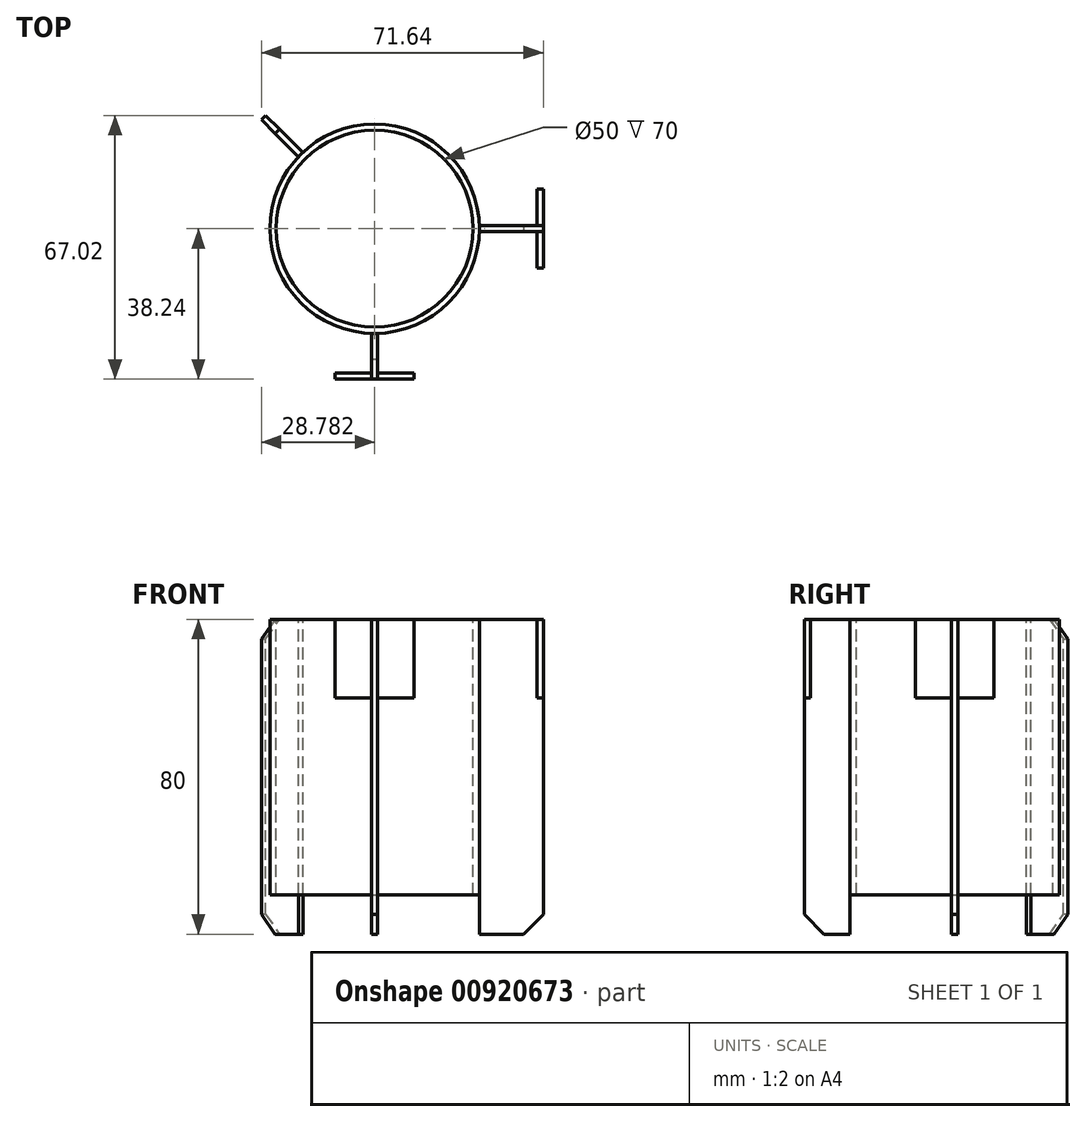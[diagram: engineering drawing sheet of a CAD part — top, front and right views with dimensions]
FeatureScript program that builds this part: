
annotation { "Feature Type Name" : "Feature", "Feature Type Description" : "" }
export const myFeature = defineFeature(function(context is Context, id is Id, definition is map)
    precondition{}
    {
        {
            var Q0;
            Q0=qCreatedBy(makeId("Top.planeOp"),FACE);
            var sketch = newSketch(context, id + "F0", { "sketchPlane" : qUnion([Q0])});
            skCircle(sketch, "E0", {"center": v(31.14, -33.92) * mm, "radius": 8 * mm});
            skLineSegment(sketch, "E1", {"start": v(31.14, -33.92) * mm, "end": v(-100.33, -33.92) * mm, "construction": true});
            skLineSegment(sketch, "E2", {"start": v(31.14, -33.92) * mm, "end": v(31.14, 79.64) * mm, "construction": true});
            skArc(sketch, "E3", {"start": v(30.64, 73.58) * mm, "mid": v(-43.22, 43.7) * mm, "end": v(-76.23, -28.8) * mm});
            skLineSegment(sketch, "E4", {"start": v(30.64, -25.94) * mm, "end": v(30.64, 73.58) * mm});
            skLineSegment(sketch, "E5", {"start": v(25, -28.8) * mm, "end": v(-76.23, -28.8) * mm});
            skArc(sketch, "E6", {"start": v(-76.23, -28.8) * mm, "mid": v(-76.32, -31.11) * mm, "end": v(-76.36, -33.42) * mm});
            skLineSegment(sketch, "E7", {"start": v(25, -28.8) * mm, "end": v(25, -28.8) * mm});
            skLineSegment(sketch, "E8.0", {"start": v(23.16, -27.2) * mm, "end": v(-74.54, -27.2) * mm});
            skArc(sketch, "E8.1", {"start": v(29.04, 71.96) * mm, "mid": v(-42.09, 42.58) * mm, "end": v(-74.54, -27.2) * mm});
            skLineSegment(sketch, "E8.2", {"start": v(29.04, -21.32) * mm, "end": v(29.04, 71.96) * mm});
            skCircle(sketch, "E9.0", {"center": v(31.14, -33.92) * mm, "radius": 9.6 * mm});
            skLineSegment(sketch, "E10", {"start": v(-69.87, 2.84) * mm, "end": v(-68.37, 2.3) * mm});
            skLineSegment(sketch, "E11", {"start": v(-58.85, -28.8) * mm, "end": v(-58.83, -27.19) * mm});
            skLineSegment(sketch, "E12", {"start": v(1.15, -28.8) * mm, "end": v(1.22, -27.2) * mm});
            skLineSegment(sketch, "E13", {"start": v(29.04, 0.62) * mm, "end": v(30.64, 0.73) * mm});
            skLineSegment(sketch, "E14", {"start": v(29.04, 60.67) * mm, "end": v(30.64, 60.7) * mm});
            skLineSegment(sketch, "E15", {"start": v(-5.62, 67.1) * mm, "end": v(-5.07, 65.6) * mm});
            skCircle(sketch, "E16", {"center": v(31.14, -33.92) * mm, "radius": 65 * mm, "construction": true});
            skLineSegment(sketch, "E17", {"start": v(31.14, -33.92) * mm, "end": v(-78.94, 76.16) * mm, "construction": true});
            skPoint(sketch, "E18", {"position": v(-14.82, 12.04) * mm});
            skCircle(sketch, "E19", {"center": v(-14.82, 12.04) * mm, "radius": 25 * mm});
            skCircle(sketch, "E20.0", {"center": v(-14.82, 12.04) * mm, "radius": 26.6 * mm});
            skLineSegment(sketch, "E21", {"start": v(-14.82, 12.04) * mm, "end": v(41.83, 12.04) * mm, "construction": true});
            skLineSegment(sketch, "E22", {"start": v(-14.82, 12.04) * mm, "end": v(-14.82, -37.35) * mm, "construction": true});
            skLineSegment(sketch, "E23", {"start": v(11.77, 12.84) * mm, "end": v(28.04, 12.84) * mm});
            skLineSegment(sketch, "E24", {"start": v(28.04, 12.84) * mm, "end": v(28.04, 11.24) * mm});
            skLineSegment(sketch, "E25", {"start": v(28.04, 11.24) * mm, "end": v(11.77, 11.24) * mm});
            skLineSegment(sketch, "E26", {"start": v(-14.02, -14.55) * mm, "end": v(-14.02, -26.2) * mm});
            skLineSegment(sketch, "E27", {"start": v(-14.02, -26.2) * mm, "end": v(-15.62, -26.2) * mm});
            skLineSegment(sketch, "E28", {"start": v(-15.62, -26.2) * mm, "end": v(-15.62, -14.55) * mm});
            skLineSegment(sketch, "E29", {"start": v(-34.18, 30.27) * mm, "end": v(-43.6, 39.69) * mm});
            skLineSegment(sketch, "E30", {"start": v(-43.6, 39.69) * mm, "end": v(-42.47, 40.82) * mm});
            skLineSegment(sketch, "E31", {"start": v(-42.47, 40.82) * mm, "end": v(-33.05, 31.4) * mm});
            skLineSegment(sketch, "E32", {"start": v(-46.34, 35.36) * mm, "end": v(-46.34, 35.36) * mm});
            skPoint(sketch, "E33", {"position": v(-14.82, -25.4) * mm});
            skLineSegment(sketch, "E34.bottom", {"start": v(-4.82, -26.2) * mm, "end": v(-24.82, -26.2) * mm});
            skLineSegment(sketch, "E34.top", {"start": v(-4.82, -24.6) * mm, "end": v(-24.82, -24.6) * mm});
            skLineSegment(sketch, "E34.left", {"start": v(-4.82, -26.2) * mm, "end": v(-4.82, -24.6) * mm});
            skLineSegment(sketch, "E34.right", {"start": v(-24.82, -26.2) * mm, "end": v(-24.82, -24.6) * mm});
            skPoint(sketch, "E35", {"position": v(27.24, 12.04) * mm});
            skLineSegment(sketch, "E36.bottom", {"start": v(28.04, 2.04) * mm, "end": v(26.44, 2.04) * mm});
            skLineSegment(sketch, "E36.top", {"start": v(28.04, 22.04) * mm, "end": v(26.44, 22.04) * mm});
            skLineSegment(sketch, "E36.left", {"start": v(28.04, 2.04) * mm, "end": v(28.04, 22.04) * mm});
            skLineSegment(sketch, "E36.right", {"start": v(26.44, 2.04) * mm, "end": v(26.44, 22.04) * mm});
            skSolve(sketch);
        }
        {
            var Q0;
            {var subQ0=sQuery(id+"F0.wireOp",EDGE,"E29");Q0=makeQuery(id+"F0.imprint","IMPRINT",FACE,{"disambiguationData":[TD([[makeQuery(id+"F0.imprint","IMPRINT",EDGE,{"derivedFrom":subQ0}),-1.0]])]});}
            var Q1;
            {var subQ0=sQuery(id+"F0.wireOp",EDGE,"E26");Q1=makeQuery(id+"F0.imprint","IMPRINT",FACE,{"disambiguationData":[TD([[makeQuery(id+"F0.imprint","IMPRINT",EDGE,{"derivedFrom":subQ0}),-1.0]])]});}
            var Q2;
            {var subQ0=sQuery(id+"F0.wireOp",EDGE,"E23");Q2=makeQuery(id+"F0.imprint","IMPRINT",FACE,{"disambiguationData":[TD([[makeQuery(id+"F0.imprint","IMPRINT",EDGE,{"derivedFrom":subQ0}),-1.0]])]});}
            extrude(context, id + "F1", {"entities" : qUnion([Q0, Q1, Q2]), "oppositeDirection" : true, "depth" : 80 * mm, "offsetDistance" : 25 * mm});
        }
        {
            var Q0;
            Q0=makeQuery(id+"F0.imprint","IMPRINT",FACE,{"disambiguationData":[TD([[makeQuery(id+"F0.imprint","IMPRINT",EDGE,{"derivedFrom":sQuery(id+"F0.wireOp",EDGE,"E19")}),-1.0]])]});
            extrude(context, id + "F2", {"entities" : qUnion([Q0]), "oppositeDirection" : true, "depth" : 70 * mm, "offsetDistance" : 25 * mm});
        }
        {
            var Q0;
            Q0=makeQuery(id+"F1.opExtrude","CAP_EDGE",EDGE,{"disambiguationData":[OSD([sQuery(id+"F0.wireOp",EDGE,"E27")])],"isStart":false});
            var Q1;
            Q1=makeQuery(id+"F1.opExtrude","CAP_EDGE",EDGE,{"disambiguationData":[OSD([sQuery(id+"F0.wireOp",EDGE,"E24")])],"isStart":false});
            var Q2;
            Q2=makeQuery(id+"F1.opExtrude","CAP_EDGE",EDGE,{"disambiguationData":[OSD([sQuery(id+"F0.wireOp",EDGE,"E30")])],"isStart":false});
            var Q3;
            Q3=makeQuery(id+"F1.opExtrude","CAP_EDGE",EDGE,{"disambiguationData":[OSD([sQuery(id+"F0.wireOp",EDGE,"E30")])],"isStart":true});
            chamfer(context, id + "F3", {"entities" : qUnion([Q0, Q1, Q2, Q3]), "width" : 5 * mm, "tangentPropagation" : true});
        }
        {
            var Q0;
            {var subQ5=sQuery(id+"F0.wireOp",EDGE,"E34.right");Q0=makeQuery(id+"F0.imprint","IMPRINT",FACE,{"disambiguationData":[TD([[makeQuery(id+"F0.imprint","IMPRINT",EDGE,{"derivedFrom":subQ5}),-1.0]])]});}
            var Q1;
            {var subQ5=sQuery(id+"F0.wireOp",EDGE,"E34.left");Q1=makeQuery(id+"F0.imprint","IMPRINT",FACE,{"disambiguationData":[TD([[makeQuery(id+"F0.imprint","IMPRINT",EDGE,{"derivedFrom":subQ5}),1.0]])]});}
            var Q2;
            {var subQ5=sQuery(id+"F0.wireOp",EDGE,"E36.bottom");Q2=makeQuery(id+"F0.imprint","IMPRINT",FACE,{"disambiguationData":[TD([[makeQuery(id+"F0.imprint","IMPRINT",EDGE,{"derivedFrom":subQ5}),-1.0]])]});}
            var Q3;
            {var subQ5=sQuery(id+"F0.wireOp",EDGE,"E36.top");Q3=makeQuery(id+"F0.imprint","IMPRINT",FACE,{"disambiguationData":[TD([[makeQuery(id+"F0.imprint","IMPRINT",EDGE,{"derivedFrom":subQ5}),1.0]])]});}
            extrude(context, id + "F4", {"entities" : qUnion([Q0, Q1, Q2, Q3]), "oppositeDirection" : true, "depth" : 20 * mm, "offsetDistance" : 25 * mm});
        }
    });
